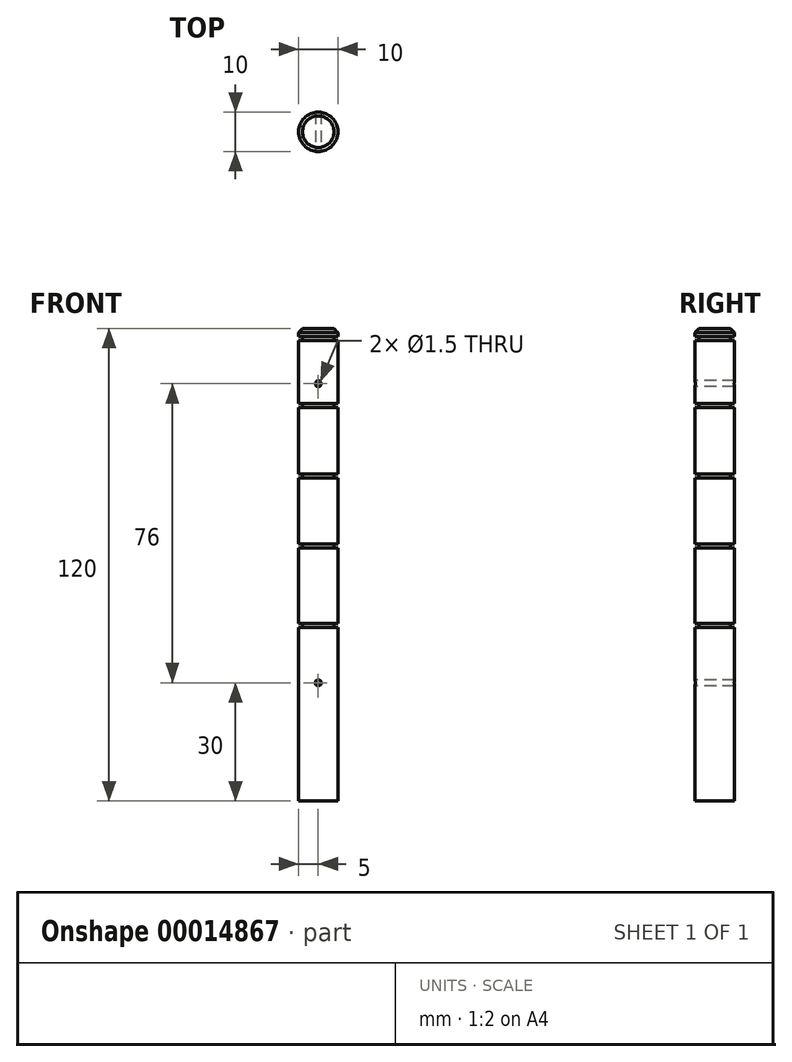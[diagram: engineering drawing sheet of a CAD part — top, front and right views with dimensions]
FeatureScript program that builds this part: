
annotation { "Feature Type Name" : "Feature", "Feature Type Description" : "" }
export const myFeature = defineFeature(function(context is Context, id is Id, definition is map)
    precondition{}
    {
        {
            var Q0;
            Q0=qCreatedBy(makeId("Top.planeOp"),FACE);
            var sketch = newSketch(context, id + "F0", { "sketchPlane" : qUnion([Q0])});
            skCircle(sketch, "E0", {"center": v(0, 0) * mm, "radius": 5 * mm});
            skSolve(sketch);
        }
        {
            var Q0;
            Q0 = qSketchRegion(id + "F0", true);
            extrude(context, id + "F1", {"entities" : qUnion([Q0]), "oppositeDirection" : true, "depth" : 120 * mm});
        }
        {
            var Q0;
            Q0=makeQuery(id+"F1.opExtrude","CAP_EDGE",EDGE,{"disambiguationData":[OSD([sQuery(id+"F0.wireOp",EDGE,"E0")])],"isStart":true});
            chamfer(context, id + "F2", {"entities" : qUnion([Q0]), "width" : 1 * mm, "tangentPropagation" : true});
        }
        {
            var Q0;
            Q0=qCreatedBy(makeId("Front.planeOp"),FACE);
            var sketch = newSketch(context, id + "F3", { "sketchPlane" : qUnion([Q0])});
            skLineSegment(sketch, "E1", {"start": v(0, 0) * mm, "end": v(0, 28.37) * mm, "construction": true});
            skLineSegment(sketch, "E2.bottom", {"start": v(5, -3) * mm, "end": v(4, -3) * mm});
            skLineSegment(sketch, "E2.top", {"start": v(5, -2) * mm, "end": v(4, -2) * mm});
            skLineSegment(sketch, "E2.left", {"start": v(5, -3) * mm, "end": v(5, -2) * mm});
            skLineSegment(sketch, "E2.right", {"start": v(4, -3) * mm, "end": v(4, -2) * mm});
            skLineSegment(sketch, "E3.MirrorCS", {"start": v(-4, -3) * mm, "end": v(-4, -2) * mm, "construction": true});
            skLineSegment(sketch, "E4.MirrorCS", {"start": v(-5, -3) * mm, "end": v(-5, -2) * mm, "construction": true});
            skLineSegment(sketch, "E5.MirrorCS", {"start": v(-5, -2) * mm, "end": v(-4, -2) * mm, "construction": true});
            skLineSegment(sketch, "E6.MirrorCS", {"start": v(-5, -3) * mm, "end": v(-4, -3) * mm, "construction": true});
            skLineSegment(sketch, "E7.0", {"start": v(-5, -120) * mm, "end": v(5, -120) * mm, "construction": true});
            skLineSegment(sketch, "E8.bottom", {"start": v(5, -19) * mm, "end": v(4, -19) * mm});
            skLineSegment(sketch, "E8.top", {"start": v(5, -20) * mm, "end": v(4, -20) * mm});
            skLineSegment(sketch, "E8.left", {"start": v(5, -19) * mm, "end": v(5, -20) * mm});
            skLineSegment(sketch, "E8.right", {"start": v(4, -19) * mm, "end": v(4, -20) * mm});
            skLineSegment(sketch, "E9.bottom", {"start": v(5, -37) * mm, "end": v(4, -37) * mm});
            skLineSegment(sketch, "E9.top", {"start": v(5, -38) * mm, "end": v(4, -38) * mm});
            skLineSegment(sketch, "E9.left", {"start": v(5, -37) * mm, "end": v(5, -38) * mm});
            skLineSegment(sketch, "E9.right", {"start": v(4, -37) * mm, "end": v(4, -38) * mm});
            skLineSegment(sketch, "E10.bottom", {"start": v(5, -54.68) * mm, "end": v(4, -54.68) * mm});
            skLineSegment(sketch, "E10.top", {"start": v(5, -55.68) * mm, "end": v(4, -55.68) * mm});
            skLineSegment(sketch, "E10.left", {"start": v(5, -54.68) * mm, "end": v(5, -55.68) * mm});
            skLineSegment(sketch, "E10.right", {"start": v(4, -54.68) * mm, "end": v(4, -55.68) * mm});
            skLineSegment(sketch, "E11.bottom", {"start": v(5, -74.98) * mm, "end": v(4, -74.98) * mm});
            skLineSegment(sketch, "E11.top", {"start": v(5, -75.98) * mm, "end": v(4, -75.98) * mm});
            skLineSegment(sketch, "E11.left", {"start": v(5, -74.98) * mm, "end": v(5, -75.98) * mm});
            skLineSegment(sketch, "E11.right", {"start": v(4, -74.98) * mm, "end": v(4, -75.98) * mm});
            skSolve(sketch);
        }
        {
            var Q0;
            Q0 = qSketchRegion(id + "F3", true);
            var Q1;
            Q1=sQuery(id+"F3.wireOp",EDGE,"E1");
            revolve(context, id + "F4", {"operationType" : NewBodyOperationType.REMOVE, "entities" : qUnion([Q0]), "axis" : qUnion([Q1]), "revolveType" : RevolveType.FULL, "oppositeDirection" : true});
        }
        {
            var Q0;
            Q0=qCreatedBy(makeId("Front.planeOp"),FACE);
            var sketch = newSketch(context, id + "F5", { "sketchPlane" : qUnion([Q0])});
            skCircle(sketch, "E12", {"center": v(0, -14) * mm, "radius": 0.75 * mm});
            skCircle(sketch, "E13", {"center": v(0, -90) * mm, "radius": 0.75 * mm});
            skSolve(sketch);
        }
        {
            var Q0;
            Q0 = qSketchRegion(id + "F5", true);
            extrude(context, id + "F6", {"entities" : qUnion([Q0]), "operationType" : NewBodyOperationType.REMOVE, "endBound" : BoundingType.SYMMETRIC, "oppositeDirection" : true, "depth" : 25 * mm});
        }
    });
